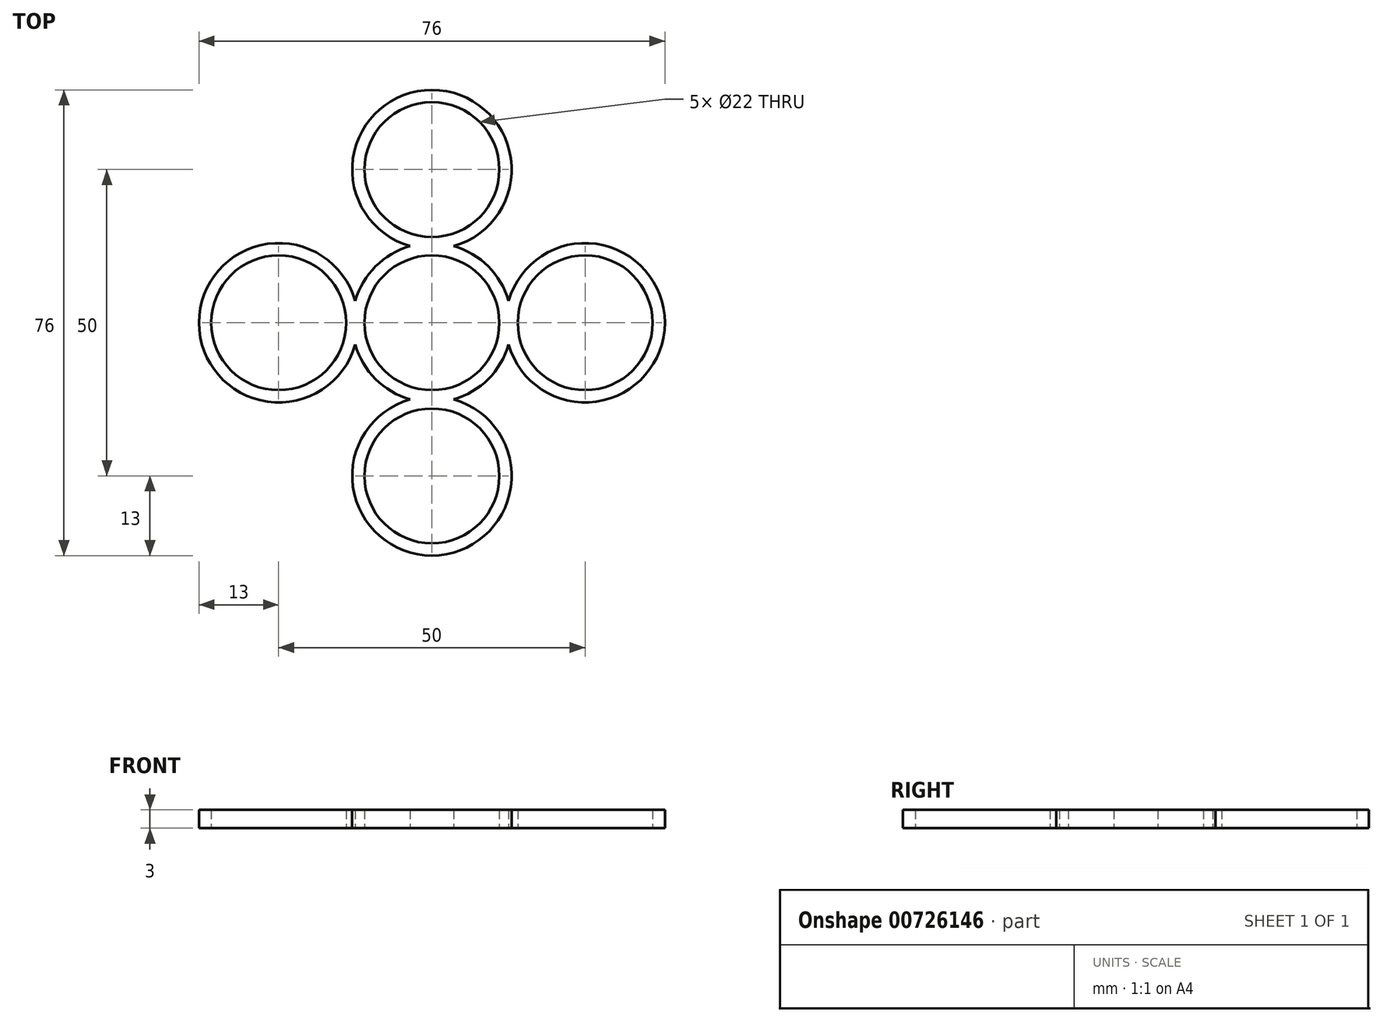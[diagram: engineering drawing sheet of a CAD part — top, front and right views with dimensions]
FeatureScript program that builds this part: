
annotation { "Feature Type Name" : "Feature", "Feature Type Description" : "" }
export const myFeature = defineFeature(function(context is Context, id is Id, definition is map)
    precondition{}
    {
        {
            var Q0;
            Q0=qCreatedBy(makeId("Top.planeOp"),FACE);
            var sketch = newSketch(context, id + "F0", { "sketchPlane" : qUnion([Q0])});
            skCircle(sketch, "E0", {"center": v(0, 0) * mm, "radius": 11 * mm});
            skArc(sketch, "E1", {"start": v(-12.5, -3.57) * mm, "mid": v(-9.2, -9.2) * mm, "end": v(-3.57, -12.5) * mm});
            skLineSegment(sketch, "E2", {"start": v(-11, 0) * mm, "end": v(-14, 0) * mm});
            skCircle(sketch, "E3", {"center": v(-25, 0) * mm, "radius": 11 * mm});
            skArc(sketch, "E4", {"start": v(-12.5, 3.57) * mm, "mid": v(-38, 0) * mm, "end": v(-12.5, -3.57) * mm});
            skLineSegment(sketch, "E5", {"start": v(11, 0) * mm, "end": v(14, 0) * mm});
            skCircle(sketch, "E6", {"center": v(25, 0) * mm, "radius": 11 * mm});
            skArc(sketch, "E7", {"start": v(12.5, -3.57) * mm, "mid": v(38, 0) * mm, "end": v(12.5, 3.57) * mm});
            skArc(sketch, "E8.trimOffspring", {"start": v(12.5, 3.57) * mm, "mid": v(9.2, 9.2) * mm, "end": v(3.57, 12.5) * mm});
            skLineSegment(sketch, "E9", {"start": v(0, 11) * mm, "end": v(0, 14) * mm});
            skCircle(sketch, "E10", {"center": v(0, 25) * mm, "radius": 11 * mm});
            skArc(sketch, "E11", {"start": v(3.57, 12.5) * mm, "mid": v(0, 38) * mm, "end": v(-3.57, 12.5) * mm});
            skArc(sketch, "E12.trimOffspring", {"start": v(-3.57, 12.5) * mm, "mid": v(-9.2, 9.2) * mm, "end": v(-12.5, 3.57) * mm});
            skLineSegment(sketch, "E13", {"start": v(0, -11) * mm, "end": v(0, -14) * mm});
            skCircle(sketch, "E14", {"center": v(0, -25) * mm, "radius": 11 * mm});
            skArc(sketch, "E15", {"start": v(-3.57, -12.5) * mm, "mid": v(0, -38) * mm, "end": v(3.57, -12.5) * mm});
            skArc(sketch, "E16.trimOffspring", {"start": v(3.57, -12.5) * mm, "mid": v(9.2, -9.2) * mm, "end": v(12.5, -3.57) * mm});
            skSolve(sketch);
        }
        {
            var Q0;
            Q0=makeQuery(id+"F0.imprint","IMPRINT",FACE,{"disambiguationData":[TD([[makeQuery(id+"F0.imprint","IMPRINT",EDGE,{"derivedFrom":sQuery(id+"F0.wireOp",EDGE,"E1")}),1.0]])]});
            extrude(context, id + "F1", {"entities" : qUnion([Q0]), "depth" : 3 * mm, "offsetDistance" : 25 * mm});
        }
    });
